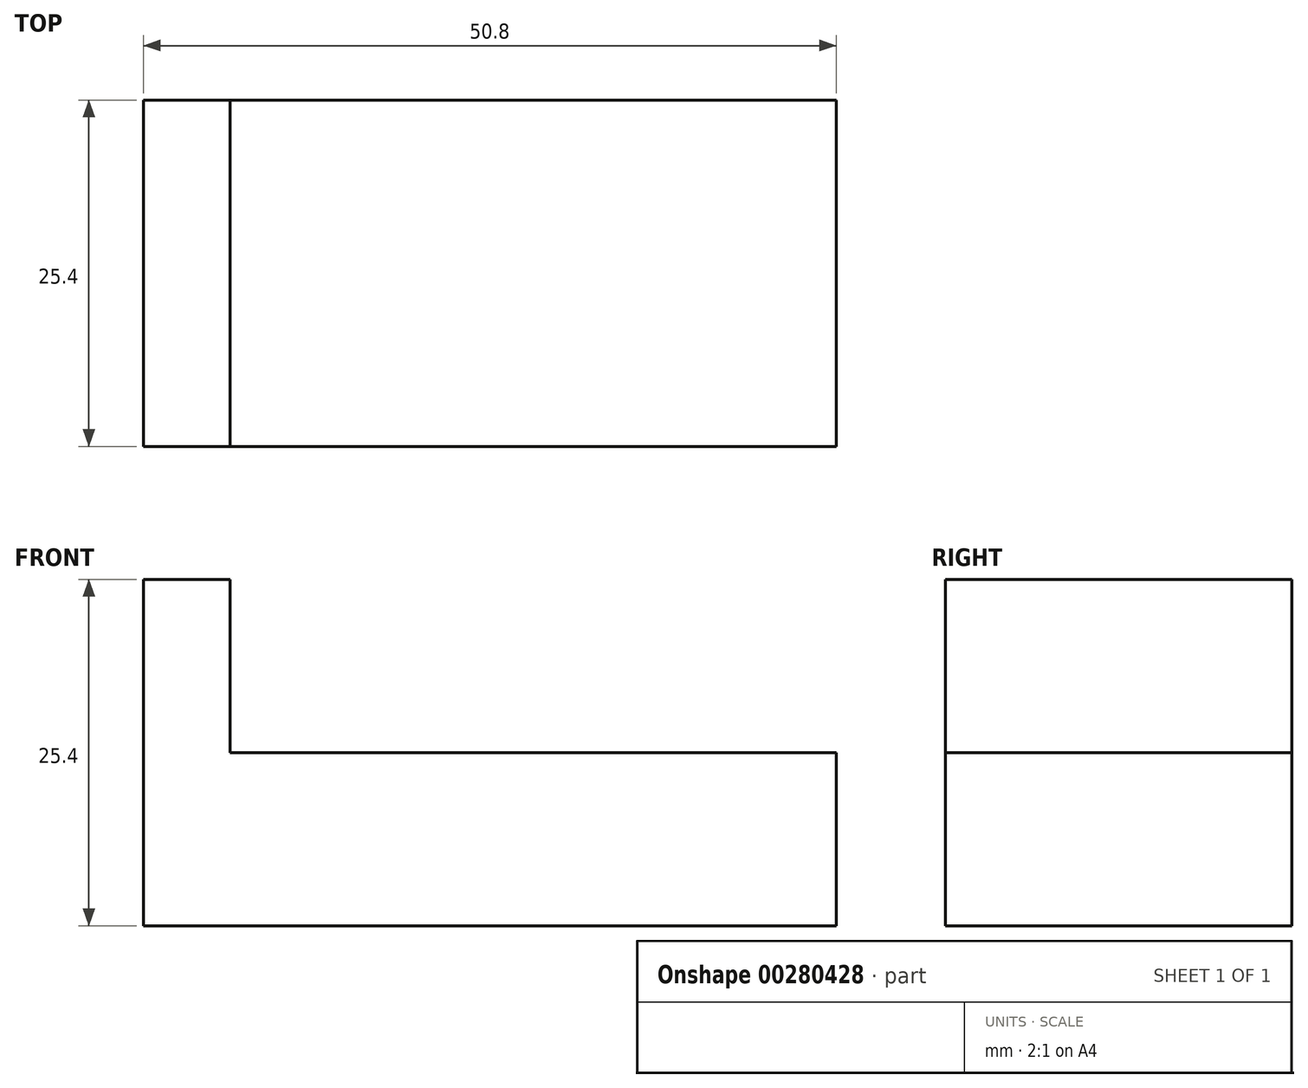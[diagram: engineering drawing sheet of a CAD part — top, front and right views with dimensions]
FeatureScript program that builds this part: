
annotation { "Feature Type Name" : "Feature", "Feature Type Description" : "" }
export const myFeature = defineFeature(function(context is Context, id is Id, definition is map)
    precondition{}
    {
        {
            var Q0;
            Q0=qCreatedBy(makeId("Front.planeOp"),FACE);
            var sketch = newSketch(context, id + "F0", { "sketchPlane" : qUnion([Q0])});
            skLineSegment(sketch, "E0", {"start": v(0, 0) * mm, "end": v(50.8, 0) * mm});
            skLineSegment(sketch, "E1", {"start": v(50.8, 0) * mm, "end": v(50.8, 12.7) * mm});
            skLineSegment(sketch, "E2", {"start": v(50.8, 12.7) * mm, "end": v(6.35, 12.7) * mm});
            skLineSegment(sketch, "E3", {"start": v(6.35, 12.7) * mm, "end": v(6.35, 25.4) * mm});
            skLineSegment(sketch, "E4", {"start": v(6.35, 25.4) * mm, "end": v(0, 25.4) * mm});
            skLineSegment(sketch, "E5", {"start": v(0, 25.4) * mm, "end": v(0, 0) * mm});
            skSolve(sketch);
        }
        {
            var Q0;
            Q0 = qSketchRegion(id + "F0", true);
            extrude(context, id + "F1", {"entities" : qUnion([Q0]), "depth" : 25.4 * mm});
        }
    });
